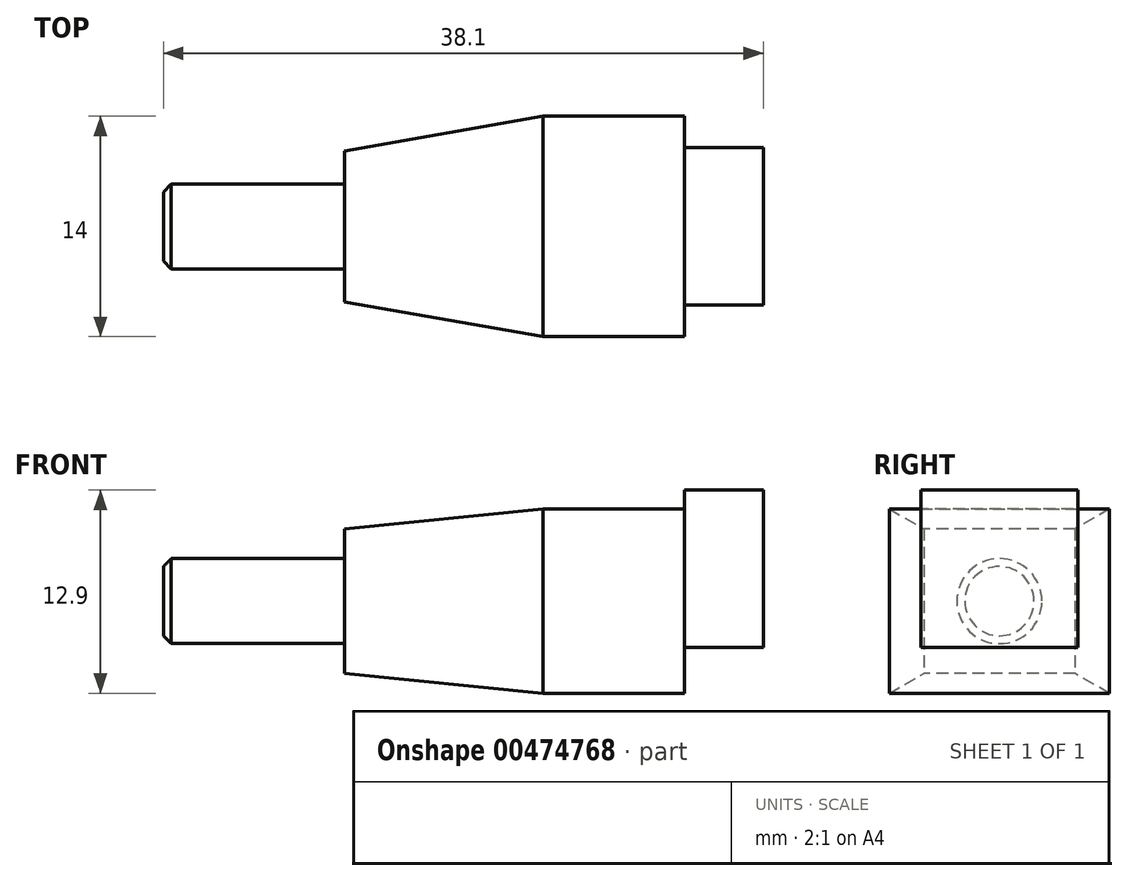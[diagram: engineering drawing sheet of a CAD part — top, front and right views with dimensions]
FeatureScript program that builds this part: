
annotation { "Feature Type Name" : "Feature", "Feature Type Description" : "" }
export const myFeature = defineFeature(function(context is Context, id is Id, definition is map)
    precondition{}
    {
        {
            var Q0;
            Q0=qCreatedBy(makeId("Top.planeOp"),FACE);
            var sketch = newSketch(context, id + "F0", { "sketchPlane" : qUnion([Q0])});
            skLineSegment(sketch, "E0", {"start": v(0, 0) * mm, "end": v(21.6, 0) * mm, "construction": true});
            skLineSegment(sketch, "E1", {"start": v(0, 0) * mm, "end": v(0, 4.8) * mm});
            skLineSegment(sketch, "E2", {"start": v(0, 4.8) * mm, "end": v(12.6, 7) * mm});
            skLineSegment(sketch, "E3", {"start": v(12.6, 7) * mm, "end": v(21.6, 7) * mm});
            skLineSegment(sketch, "E4", {"start": v(21.6, 7) * mm, "end": v(21.6, 0) * mm});
            skLineSegment(sketch, "E5.MirrorCS", {"start": v(0, 0) * mm, "end": v(0, -4.8) * mm});
            skLineSegment(sketch, "E6.MirrorCS", {"start": v(0, -4.8) * mm, "end": v(12.6, -7) * mm});
            skLineSegment(sketch, "E7.MirrorCS", {"start": v(12.6, -7) * mm, "end": v(21.6, -7) * mm});
            skLineSegment(sketch, "E8.MirrorCS", {"start": v(21.6, -7) * mm, "end": v(21.6, 0) * mm});
            skSolve(sketch);
        }
        {
            var Q0;
            Q0 = qSketchRegion(id + "F0", true);
            extrude(context, id + "F1", {"entities" : qUnion([Q0]), "depth" : 11.7 * mm});
        }
        {
            var Q0;
            Q0=makeQuery(id+"F1.opExtrude","SWEPT_FACE",FACE,{"disambiguationData":[OSD([sQuery(id+"F0.wireOp",EDGE,"E7.MirrorCS")])]});
            var sketch = newSketch(context, id + "F2", { "sketchPlane" : qUnion([Q0])});
            skLineSegment(sketch, "E9", {"start": v(12.6, 11.7) * mm, "end": v(0, 11.7) * mm});
            skLineSegment(sketch, "E10", {"start": v(0, 11.7) * mm, "end": v(0, 10.45) * mm});
            skLineSegment(sketch, "E11", {"start": v(0, 10.45) * mm, "end": v(12.6, 11.7) * mm});
            skLineSegment(sketch, "E12", {"start": v(12.6, 0) * mm, "end": v(0, 0) * mm});
            skLineSegment(sketch, "E13", {"start": v(0, 0) * mm, "end": v(0, 1.25) * mm});
            skLineSegment(sketch, "E14", {"start": v(0, 1.25) * mm, "end": v(12.6, 0) * mm});
            skSolve(sketch);
        }
        {
            var Q0;
            Q0 = qSketchRegion(id + "F2", true);
            var Q1;
            Q1=makeQuery(id+"F1.opExtrude","SWEPT_FACE",FACE,{"disambiguationData":[OSD([sQuery(id+"F0.wireOp",EDGE,"E3")])]});
            extrude(context, id + "F3", {"entities" : qUnion([Q0]), "operationType" : NewBodyOperationType.REMOVE, "endBound" : BoundingType.UP_TO_SURFACE, "oppositeDirection" : true, "endBoundEntityFace" : qUnion([Q1]), "depth" : 25 * mm});
        }
        {
            var Q0;
            Q0=makeQuery(id+"F1.opExtrude","SWEPT_FACE",FACE,{"disambiguationData":[OSD([sQuery(id+"F0.wireOp",EDGE,"E1"),sQuery(id+"F0.wireOp",EDGE,"E5.MirrorCS")])]});
            var sketch = newSketch(context, id + "F4", { "sketchPlane" : qUnion([Q0])});
            skCircle(sketch, "E15", {"center": v(0, 5.85) * mm, "radius": 2.7 * mm});
            skSolve(sketch);
        }
        {
            var Q0;
            Q0 = qSketchRegion(id + "F4", true);
            extrude(context, id + "F5", {"entities" : qUnion([Q0]), "operationType" : NewBodyOperationType.ADD, "depth" : 11.5 * mm});
        }
        {
            var Q0;
            Q0=makeQuery(id+"F5.opExtrude","CAP_EDGE",EDGE,{"disambiguationData":[OSD([sQuery(id+"F4.wireOp",EDGE,"E15")])],"isStart":false});
            chamfer(context, id + "F6", {"entities" : qUnion([Q0]), "width" : 0.5 * mm, "tangentPropagation" : true});
        }
        {
            var Q0;
            Q0=makeQuery(id+"F1.opExtrude","SWEPT_FACE",FACE,{"disambiguationData":[OSD([sQuery(id+"F0.wireOp",EDGE,"E4"),sQuery(id+"F0.wireOp",EDGE,"E8.MirrorCS")])]});
            var sketch = newSketch(context, id + "F7", { "sketchPlane" : qUnion([Q0])});
            skLineSegment(sketch, "E16.bottom", {"start": v(-5, 2.9) * mm, "end": v(5, 2.9) * mm});
            skLineSegment(sketch, "E16.top", {"start": v(-5, 12.9) * mm, "end": v(5, 12.9) * mm});
            skLineSegment(sketch, "E16.left", {"start": v(-5, 2.9) * mm, "end": v(-5, 12.9) * mm});
            skLineSegment(sketch, "E16.right", {"start": v(5, 2.9) * mm, "end": v(5, 12.9) * mm});
            skSolve(sketch);
        }
        {
            var Q0;
            Q0 = qSketchRegion(id + "F7", true);
            extrude(context, id + "F8", {"entities" : qUnion([Q0]), "operationType" : NewBodyOperationType.ADD, "depth" : 5 * mm});
        }
    });
